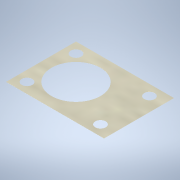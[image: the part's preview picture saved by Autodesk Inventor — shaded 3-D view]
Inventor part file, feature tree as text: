
AUTODESK INVENTOR PART (.ipt)
format: ipt  version: 2022 (Build 260153000, 153)  size: 133,632 bytes
history: native  units: mm
features: extrude x2, sketch x2, other x2, reference x1
ambient origin geometry x8: Origin, YZ Plane, XZ Plane, XY Plane, X Axis, Y Axis, Z Axis, Center Point
bodies: Solid1 (feature_tree)
feature tree (7):
  extrude  "Extrusion1"  Depth=20.0mm
  extrude  "Extrusion2"  Depth=0.01mm
  sketch  "Sketch1"  dims[d0=28.0mm d1=20.0mm]
  sketch  "Sketch2"  dims[d6=3.0mm d7=3.0mm d8=0.01mm d9=0.0mm d10=0.5mm d11=0.0mm]
  reference  "Reference1"
  other  "Assembly1"
  other  "MOTORBLOCK PART 3:1"
